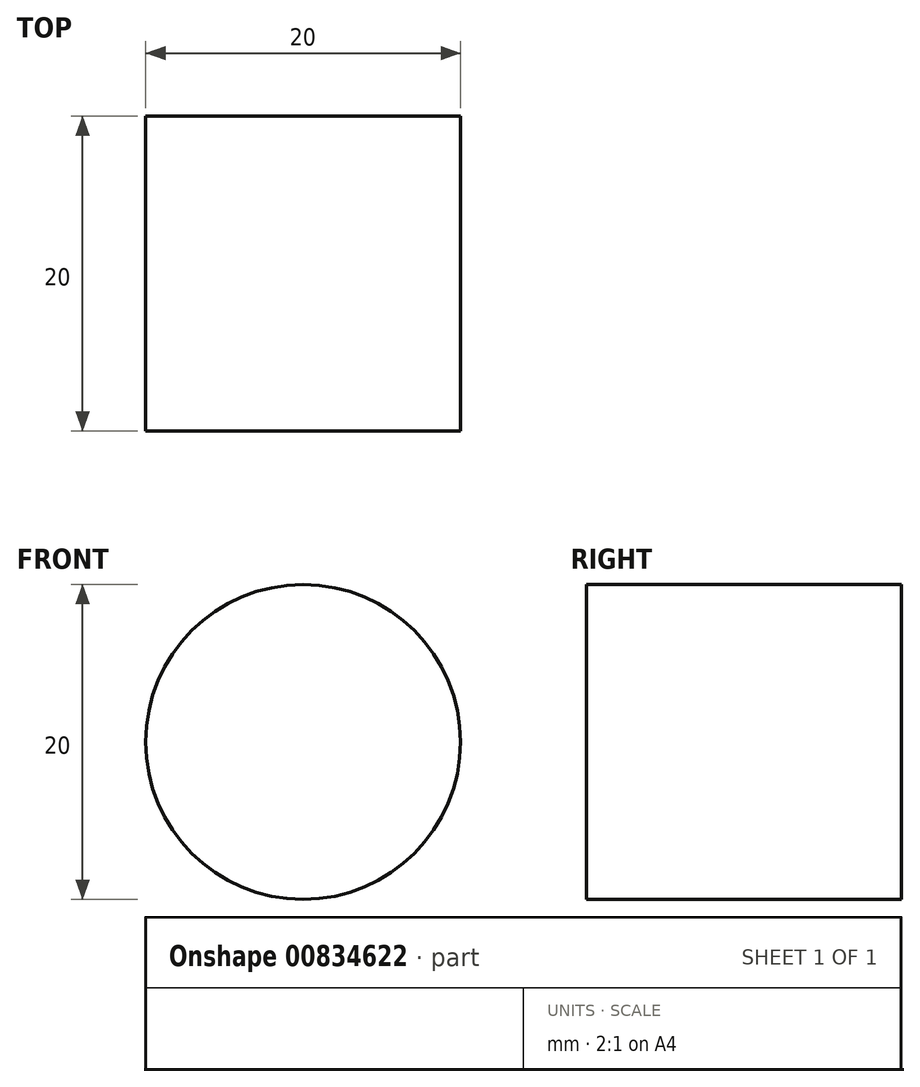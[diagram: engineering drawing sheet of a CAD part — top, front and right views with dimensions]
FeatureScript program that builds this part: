
annotation { "Feature Type Name" : "Feature", "Feature Type Description" : "" }
export const myFeature = defineFeature(function(context is Context, id is Id, definition is map)
    precondition{}
    {
        {
            var Q0;
            Q0=qCreatedBy(makeId("Front.planeOp"),FACE);
            var sketch = newSketch(context, id + "F0", { "sketchPlane" : qUnion([Q0])});
            skCircle(sketch, "E0", {"center": v(-32, 38) * mm, "radius": 10 * mm});
            skSolve(sketch);
        }
        {
            var Q0;
            Q0 = qSketchRegion(id + "F0", true);
            extrude(context, id + "F1", {"entities" : qUnion([Q0]), "depth" : 20 * mm, "offsetDistance" : 25 * mm});
        }
    });
